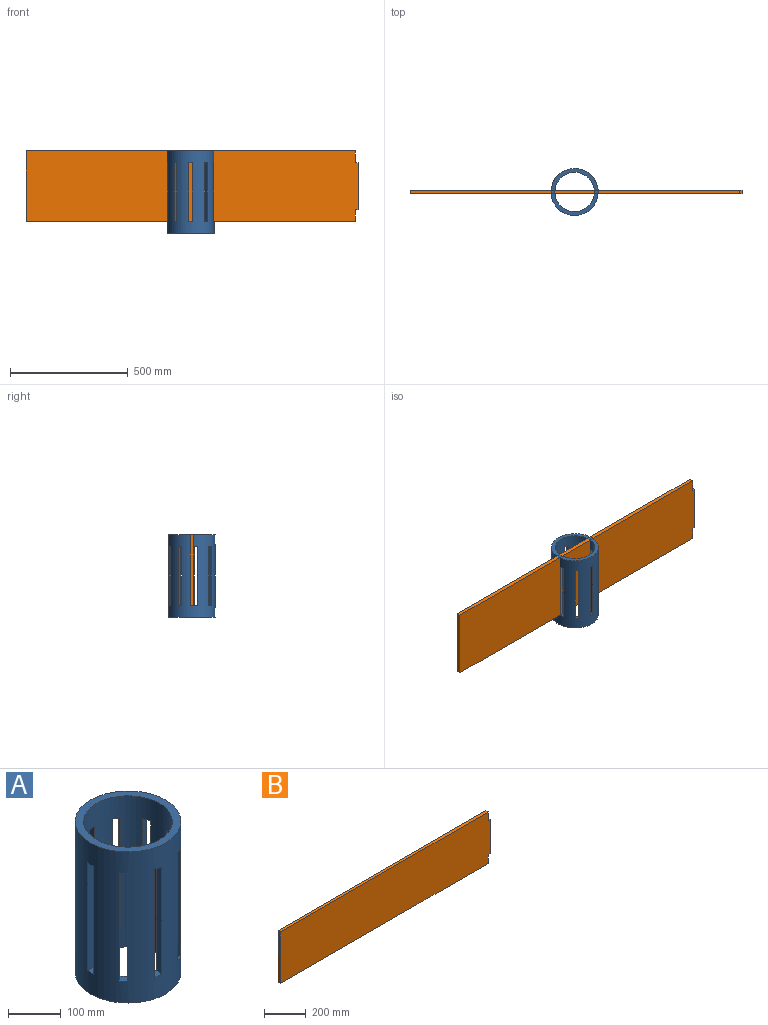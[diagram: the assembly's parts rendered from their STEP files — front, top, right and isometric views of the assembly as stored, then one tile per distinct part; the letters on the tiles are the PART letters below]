
ASSEMBLY  parts=2 mates=1
PART A: 40 faces, bbox 200x200x350 mm
  f0: plane 22.59x22.58mm, normal (0,0,-1), area 256.3mm2, adj f1,f3,f32,f33
  f1: plane 250x12.3mm, normal (0.64,0.77,0), area 4015.3mm2, adj f0,f2,f32,f33
  f2: plane 22.59x22.58mm, normal (0,0,1), area 256.3mm2, adj f1,f3,f32,f33
  f3: plane 250x12.3mm, normal (-0.64,-0.77,0), area 4015.3mm2, adj f0,f2,f32,f33
  f4: plane 18.6x18.55mm, normal (0,0,-1), area 256.3mm2, adj f5,f7,f32,f33
  f5: plane 250x15.82mm, normal (0.98,0.17,0), area 4015.3mm2, adj f4,f6,f32,f33
  f6: plane 18.6x18.55mm, normal (0,0,1), area 256.3mm2, adj f5,f7,f32,f33
  f7: plane 250x15.82mm, normal (-0.98,-0.17,0), area 4015.3mm2, adj f4,f6,f32,f33
  f8: plane 21.91x21.89mm, normal (0,0,-1), area 256.3mm2, adj f9,f11,f32,f33
  f9: plane 250x13.91mm, normal (0.87,-0.5,0), area 4015.3mm2, adj f8,f10,f32,f33
  f10: plane 21.91x21.89mm, normal (0,0,1), area 256.3mm2, adj f9,f11,f32,f33
  f11: plane 250x13.91mm, normal (-0.87,0.5,0), area 4015.3mm2, adj f8,f10,f32,f33
  f12: plane 20.57x20.53mm, normal (0,0,-1), area 256.3mm2, adj f13,f15,f32,f33
  f13: plane 250x15.09mm, normal (0.34,-0.94,0), area 4015.3mm2, adj f12,f14,f32,f33
  f14: plane 20.57x20.53mm, normal (0,0,1), area 256.3mm2, adj f13,f15,f32,f33
  f15: plane 250x15.09mm, normal (-0.34,0.94,0), area 4015.3mm2, adj f12,f14,f32,f33
  f16: plane 20.57x20.53mm, normal (0,0,-1), area 256.3mm2, adj f17,f19,f32,f33
  f17: plane 250x15.09mm, normal (-0.34,-0.94,0), area 4015.3mm2, adj f16,f18,f32,f33
  f18: plane 20.57x20.53mm, normal (0,0,1), area 256.3mm2, adj f17,f19,f32,f33
  f19: plane 250x15.09mm, normal (0.34,0.94,0), area 4015.3mm2, adj f16,f18,f32,f33
  f20: plane 21.91x21.89mm, normal (0,0,-1), area 256.3mm2, adj f21,f23,f32,f33
  f21: plane 250x13.91mm, normal (-0.87,-0.5,0), area 4015.3mm2, adj f20,f22,f32,f33
  f22: plane 21.91x21.89mm, normal (0,0,1), area 256.3mm2, adj f21,f23,f32,f33
  f23: plane 250x13.91mm, normal (0.87,0.5,0), area 4015.3mm2, adj f20,f22,f32,f33
  f24: plane 18.6x18.55mm, normal (0,0,-1), area 256.3mm2, adj f25,f27,f32,f33
  f25: plane 250x15.82mm, normal (-0.98,0.17,0), area 4015.3mm2, adj f24,f26,f32,f33
  f26: plane 18.6x18.55mm, normal (0,0,1), area 256.3mm2, adj f25,f27,f32,f33
  f27: plane 250x15.82mm, normal (0.98,-0.17,0), area 4015.3mm2, adj f24,f26,f32,f33
  f28: plane 22.59x22.58mm, normal (0,0,-1), area 256.3mm2, adj f29,f31,f32,f33
  f29: plane 250x12.3mm, normal (-0.64,0.77,0), area 4015.3mm2, adj f28,f30,f32,f33
  f30: plane 22.59x22.58mm, normal (0,0,1), area 256.3mm2, adj f29,f31,f32,f33
  f31: plane 250x12.3mm, normal (0.64,-0.77,0), area 4015.3mm2, adj f28,f30,f32,f33
  f32: cylinder r=84mm len=350mm, axis (0,0,-1), area 148671mm2, adj f0,f1,f2,f3,f4,f5,f6,f7
  f33: cylinder r=100mm len=350mm, axis (0,0,-1), area 183873mm2, adj f0,f1,f2,f3,f4,f5,f6,f7
  f34: plane 200x200mm, normal (0,0,1), area 9248.8mm2, adj f32,f33
  f35: plane 200x200mm, normal (0,0,-1), area 9248.8mm2, adj f32,f33
  f36: plane 16.38x16mm, normal (0,0,-1), area 256.3mm2, adj f32,f33,f37,f39
  f37: plane 250x16.06mm, normal (0,1,0), area 4015.3mm2, adj f32,f33,f36,f38
  f38: plane 16.38x16mm, normal (0,0,1), area 256.3mm2, adj f32,f33,f37,f39
  f39: plane 250x16.06mm, normal (0,-1,0), area 4015.3mm2, adj f32,f33,f36,f38
PART B: 10 faces, bbox 1412x16x300 mm
  f0: plane 200x16mm, normal (1,0,0), area 3200mm2, adj f1,f7,f8,f9
  f1: plane 16x12mm, normal (0,0,1), area 192mm2, adj f0,f2,f8,f9
  f2: plane 50x16mm, normal (1,0,0), area 800mm2, adj f1,f3,f8,f9
  f3: plane 1400x16mm, normal (0,0,1), area 22400mm2, adj f2,f4,f8,f9
  f4: plane 300x16mm, normal (-1,0,0), area 4800mm2, adj f3,f5,f8,f9
  f5: plane 1400x16mm, normal (0,0,-1), area 22400mm2, adj f4,f6,f8,f9
  f6: plane 50x16mm, normal (1,0,0), area 800mm2, adj f5,f7,f8,f9
  f7: plane 16x12mm, normal (0,0,-1), area 192mm2, adj f0,f6,f8,f9
  f8: plane 1412x300mm, normal (0,-1,0), area 422400mm2, adj f0,f1,f2,f3,f4,f5,f6,f7
  f9: plane 1412x300mm, normal (0,1,0), area 422400mm2, adj f0,f1,f2,f3,f4,f5,f6,f7
PLACE A rot(axis=(0.71,0.71,0),180deg) t=(-672.44,-730.74,408.39)mm
PLACE B t=(127.56,-730.74,259.94)mm
MATE planar A.f33 <-> B.f3  axis (0,0,1) through (-672.44,-730.74,408.39)mm
